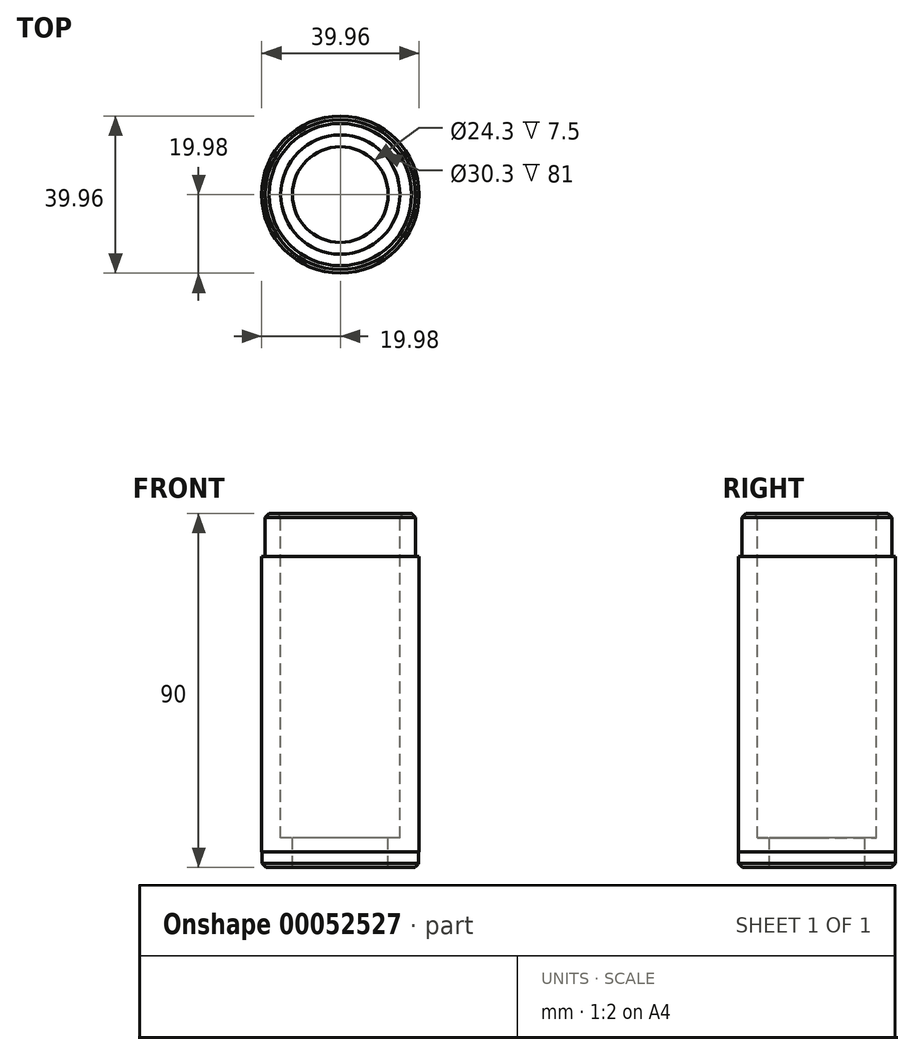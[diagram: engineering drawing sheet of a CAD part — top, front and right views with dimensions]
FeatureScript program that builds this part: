
annotation { "Feature Type Name" : "Feature", "Feature Type Description" : "" }
export const myFeature = defineFeature(function(context is Context, id is Id, definition is map)
    precondition{}
    {
        {
            var Q0;
            Q0=qCreatedBy(makeId("Front.planeOp"),FACE);
            var sketch = newSketch(context, id + "F0", { "sketchPlane" : qUnion([Q0])});
            skLineSegment(sketch, "E0.rect.bottom", {"start": v(19.08, 45) * mm, "end": v(-19.08, 45) * mm});
            skLineSegment(sketch, "E0.rect.top", {"start": v(19.9, -45) * mm, "end": v(-19.9, -45) * mm});
            skLineSegment(sketch, "E0.rect.left", {"start": v(19.98, 34) * mm, "end": v(19.98, -41) * mm});
            skLineSegment(sketch, "E0.rect.right", {"start": v(-19.98, 34) * mm, "end": v(-19.98, -41) * mm});
            skPoint(sketch, "E0.rect.middle", {"position": v(0, 0) * mm});
            skLineSegment(sketch, "E1", {"start": v(-19.07, 45) * mm, "end": v(-19.07, 34) * mm});
            skLineSegment(sketch, "E2", {"start": v(-19.07, 34) * mm, "end": v(-19.98, 34) * mm});
            skLineSegment(sketch, "E3.MirrorCS", {"start": v(19.07, 45) * mm, "end": v(19.07, 34) * mm});
            skLineSegment(sketch, "E4.MirrorCS", {"start": v(19.07, 34) * mm, "end": v(19.98, 34) * mm});
            skLineSegment(sketch, "E5", {"start": v(-12.15, -45) * mm, "end": v(-12.15, -37.5) * mm});
            skLineSegment(sketch, "E6", {"start": v(-12.15, -37.5) * mm, "end": v(-15.15, -37.5) * mm});
            skLineSegment(sketch, "E7.MirrorCS", {"start": v(12.15, -37.5) * mm, "end": v(15.15, -37.5) * mm});
            skLineSegment(sketch, "E8.MirrorCS", {"start": v(12.15, -45) * mm, "end": v(12.15, -37.5) * mm});
            skLineSegment(sketch, "E9", {"start": v(-15.15, 45) * mm, "end": v(-15.15, -37.5) * mm});
            skLineSegment(sketch, "E10.MirrorCS", {"start": v(15.15, 45) * mm, "end": v(15.15, -37.5) * mm});
            skPoint(sketch, "E11.orphan", {"position": v(-19.97, -37.5) * mm});
            skPoint(sketch, "E12.orphan", {"position": v(19.97, -37.5) * mm});
            skPoint(sketch, "E13.orphan", {"position": v(-19.98, 45) * mm});
            skPoint(sketch, "E14.orphan", {"position": v(19.98, 45) * mm});
            skLineSegment(sketch, "E15", {"start": v(-19.9, -45) * mm, "end": v(-19.9, -41) * mm});
            skLineSegment(sketch, "E16", {"start": v(-19.9, -41) * mm, "end": v(-19.97, -41) * mm});
            skLineSegment(sketch, "E17.MirrorCS", {"start": v(19.9, -45) * mm, "end": v(19.9, -41) * mm});
            skLineSegment(sketch, "E18.MirrorCS", {"start": v(19.9, -41) * mm, "end": v(19.97, -41) * mm});
            skPoint(sketch, "E19.orphan", {"position": v(-19.97, -45) * mm});
            skPoint(sketch, "E20.orphan", {"position": v(19.97, -45) * mm});
            skLineSegment(sketch, "E21", {"start": v(0, 74.12) * mm, "end": v(0, -75.69) * mm});
            skSolve(sketch);
        }
        {
            var Q0;
            Q0=makeQuery(id+"F0.imprint","IMPRINT",FACE,{"disambiguationData":[TD([[makeQuery(id+"F0.imprint","IMPRINT",EDGE,{"derivedFrom":sQuery(id+"F0.wireOp",EDGE,"E0.rect.right")}),1.0]])]});
            var Q1;
            Q1=sQuery(id+"F0.wireOp",EDGE,"E21");
            revolve(context, id + "F1", {"entities" : qUnion([Q0]), "axis" : qUnion([Q1]), "revolveType" : RevolveType.FULL});
        }
        {
            var Q0;
            Q0=makeQuery(id+"F1.opRevolve","SWEPT_EDGE",EDGE,{"disambiguationData":[OSD([sQuery(id+"F0.wireOp",EDGE,"E0.rect.bottom"),sQuery(id+"F0.wireOp",EDGE,"E9")])]});
            fillet(context, id + "F2", {"entities" : qUnion([Q0]), "radius" : 1.5 * mm, "tangentPropagation" : true, "allowEdgeOverflow" : false});
        }
        {
            var Q0;
            Q0=makeQuery(id+"F1.opRevolve","SWEPT_EDGE",EDGE,{"disambiguationData":[OSD([sQuery(id+"F0.wireOp",EDGE,"E0.rect.bottom"),sQuery(id+"F0.wireOp",EDGE,"E1")])]});
            var Q1;
            Q1=makeQuery(id+"F1.opRevolve","SWEPT_EDGE",EDGE,{"disambiguationData":[OSD([sQuery(id+"F0.wireOp",EDGE,"E0.rect.top"),sQuery(id+"F0.wireOp",EDGE,"E15")])]});
            chamfer(context, id + "F3", {"entities" : qUnion([Q0, Q1]), "width" : 1 * mm, "tangentPropagation" : true});
        }
    });
